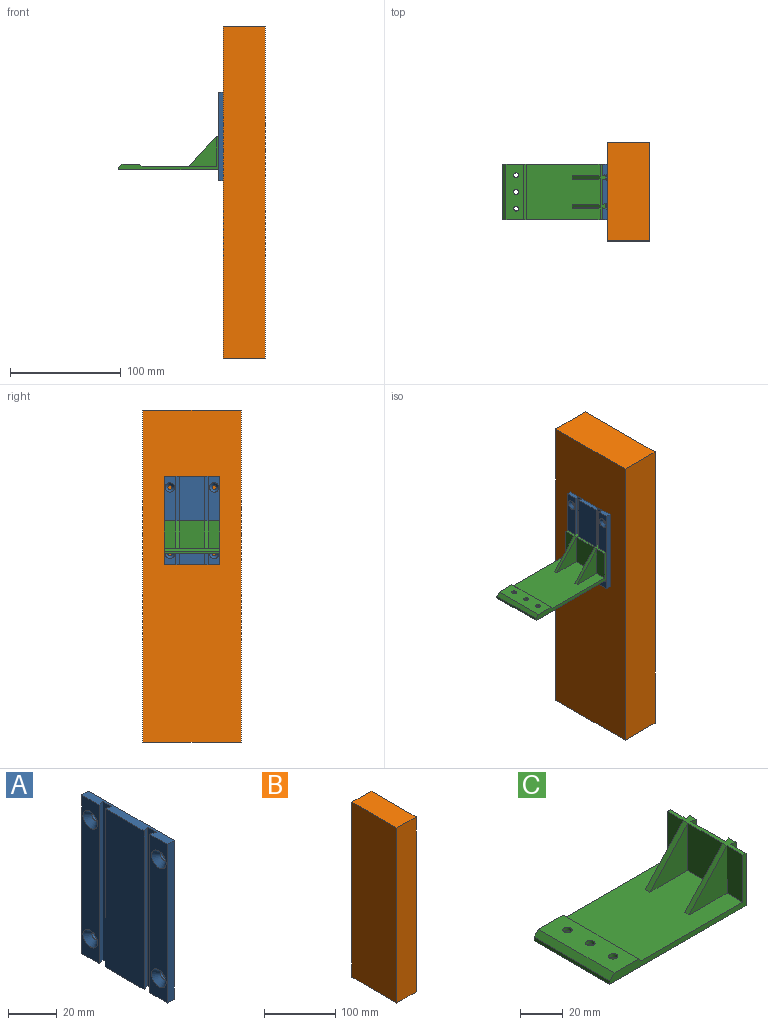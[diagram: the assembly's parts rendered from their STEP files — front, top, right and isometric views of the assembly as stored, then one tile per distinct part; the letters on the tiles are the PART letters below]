
ASSEMBLY  parts=3 mates=2
PART A: 22 faces, bbox 4x50x80 mm
  f0: plane 80x4mm, normal (0,1,0), area 320mm2, adj f1,f11,f12,f13
  f1: plane 80x10.36mm, normal (-1,0,0), area 715.4mm2, adj f0,f2,f12,f13,f15,f21
  f2: plane 80x3mm, normal (0.32,-0.95,0), area 253mm2, adj f1,f3,f12,f13
  f3: plane 80x5.28mm, normal (-1,0,0), area 422.2mm2, adj f2,f4,f12,f13
  f4: plane 80x3mm, normal (0.32,0.95,0), area 253mm2, adj f3,f5,f12,f13
  f5: plane 80x22.72mm, normal (-1,0,0), area 1817.8mm2, adj f4,f6,f12,f13
  f6: plane 80x3mm, normal (0.32,-0.95,0), area 253mm2, adj f5,f7,f12,f13
  f7: plane 80x5.28mm, normal (-1,0,0), area 422.2mm2, adj f6,f8,f12,f13
  f8: plane 80x3mm, normal (0.32,0.95,0), area 253mm2, adj f7,f9,f12,f13
  f9: plane 80x10.36mm, normal (-1,0,0), area 715.4mm2, adj f8,f10,f12,f13,f17,f19
  f10: plane 80x4mm, normal (0,-1,0), area 320mm2, adj f9,f11,f12,f13
  f11: plane 80x50mm, normal (1,0,0), area 3958mm2, adj f0,f10,f12,f13,f14,f16,f18,f20
  f12: plane 50x4mm, normal (0,0,1), area 174.3mm2, adj f0,f1,f2,f3,f4,f5,f6,f7
  f13: plane 50x4mm, normal (0,0,-1), area 174.3mm2, adj f0,f1,f2,f3,f4,f5,f6,f7
  f14: cylinder r=1.83mm len=3.66mm, axis (-1,0,0), area 14mm2, adj f11,f15
  f15: cone r=1.83mm half-angle=41deg, axis (-1,0,0), area 70.5mm2, adj f1,f14
  f16: cylinder r=1.83mm len=3.66mm, axis (-1,0,0), area 14mm2, adj f11,f17
  f17: cone r=1.83mm half-angle=41deg, axis (-1,0,0), area 70.5mm2, adj f9,f16
  f18: cylinder r=1.83mm len=3.66mm, axis (-1,0,0), area 14mm2, adj f11,f19
  f19: cone r=1.83mm half-angle=41deg, axis (-1,0,0), area 70.5mm2, adj f9,f18
  f20: cylinder r=1.83mm len=3.66mm, axis (-1,0,0), area 14mm2, adj f11,f21
  f21: cone r=1.83mm half-angle=41deg, axis (-1,0,0), area 70.5mm2, adj f1,f20
PART B: 6 faces, bbox 38.1x88.9x300 mm
  f0: plane 300x38.1mm, normal (0,1,0), area 11430mm2, adj f1,f3,f4,f5
  f1: plane 300x88.9mm, normal (-1,0,0), area 26670mm2, adj f0,f2,f4,f5
  f2: plane 300x38.1mm, normal (0,-1,0), area 11430mm2, adj f1,f3,f4,f5
  f3: plane 300x88.9mm, normal (1,0,0), area 26670mm2, adj f0,f2,f4,f5
  f4: plane 88.9x38.1mm, normal (0,0,1), area 3387.1mm2, adj f0,f1,f2,f3
  f5: plane 88.9x38.1mm, normal (0,0,-1), area 3387.1mm2, adj f0,f1,f2,f3
PART C: 33 faces, bbox 93x50x30 mm
  f0: plane 27x10.5mm, normal (-1,0,0), area 283.5mm2, adj f1,f5,f14,f27
  f1: plane 66.8x50mm, normal (0,0,1), area 3190mm2, adj f0,f2,f5,f7,f15,f22,f23,f24
  f2: plane 27x23mm, normal (-1,0,0), area 621mm2, adj f1,f14,f23,f26
  f3: plane 30x10.5mm, normal (1,0,0), area 315mm2, adj f7,f12,f14,f20
  f4: plane 30x23mm, normal (1,0,0), area 690mm2, adj f12,f14,f17,f19
  f5: plane 90x30mm, normal (0,-1,0), area 359.9mm2, adj f0,f1,f6,f11,f12,f13,f14,f31
  f6: plane 30x10.5mm, normal (1,0,0), area 315mm2, adj f5,f12,f14,f18
  f7: plane 90x30mm, normal (0,1,0), area 359.9mm2, adj f1,f3,f11,f12,f13,f14,f15,f31
  f8: cylinder r=2.2mm len=4.4mm, axis (0,0,-1), area 27.6mm2, adj f13,f29
  f9: cylinder r=2.2mm len=4.4mm, axis (0,0,-1), area 27.6mm2, adj f13,f30
  f10: cylinder r=2.2mm len=4.4mm, axis (0,0,-1), area 27.6mm2, adj f13,f28
  f11: plane 50x2mm, normal (-1,0,0), area 100mm2, adj f5,f7,f12,f32
  f12: plane 93x50mm, normal (0,0,-1), area 4269.2mm2, adj f3,f4,f5,f6,f7,f11,f16,f17
  f13: plane 50x16.2mm, normal (0,0,1), area 764.4mm2, adj f5,f7,f8,f9,f10,f31,f32
  f14: plane 50x5mm, normal (0,0,1), area 124mm2, adj f0,f2,f3,f4,f5,f6,f7,f15
  f15: plane 27x10.5mm, normal (-1,0,0), area 283.5mm2, adj f1,f7,f14,f24
  f16: plane 30x5mm, normal (1,0,0), area 150mm2, adj f12,f14,f17,f18
  f17: plane 30x3mm, normal (-0.32,0.95,0), area 94.9mm2, adj f4,f12,f14,f16
  f18: plane 30x3mm, normal (-0.32,-0.95,0), area 94.9mm2, adj f6,f12,f14,f16
  f19: plane 30x3mm, normal (-0.32,-0.95,0), area 94.9mm2, adj f4,f12,f14,f21
  f20: plane 30x3mm, normal (-0.32,0.95,0), area 94.9mm2, adj f3,f12,f14,f21
  f21: plane 30x5mm, normal (1,0,0), area 150mm2, adj f12,f14,f19,f20
  f22: plane 27x25mm, normal (-0.73,0,0.68), area 110.4mm2, adj f1,f14,f23,f24
  f23: plane 27x25mm, normal (0,-1,0), area 337.5mm2, adj f1,f2,f22
  f24: plane 27x25mm, normal (0,1,0), area 337.5mm2, adj f1,f15,f22
  f25: plane 27x25mm, normal (-0.73,0,0.68), area 110.4mm2, adj f1,f14,f26,f27
  f26: plane 27x25mm, normal (0,1,0), area 337.5mm2, adj f1,f2,f25
  f27: plane 27x25mm, normal (0,-1,0), area 337.5mm2, adj f0,f1,f25
  f28: cone r=2.2mm half-angle=45deg, axis (0,0,-1), area 98.6mm2, adj f10,f12
  f29: cone r=5.2mm half-angle=45deg, axis (0,0,-1), area 98.6mm2, adj f8,f12
  f30: cone r=5.2mm half-angle=45deg, axis (0,0,-1), area 98.6mm2, adj f9,f12
  f31: plane 50x2mm, normal (0.71,0,0.71), area 141.4mm2, adj f1,f5,f7,f13
  f32: plane 50x3mm, normal (-0.71,0,0.71), area 212.1mm2, adj f5,f7,f11,f13
PLACE A t=(0,0,160)mm
PLACE B at identity fixed
PLACE C t=(-0.4,0,170)mm
MATE fastened B.f1 <-> A.f11  axis (-1,0,0) through (4.1,0,150)mm
MATE slider C.f14 <-> A.f12  axis (0,0,1) through (2.6,-13,200)mm
